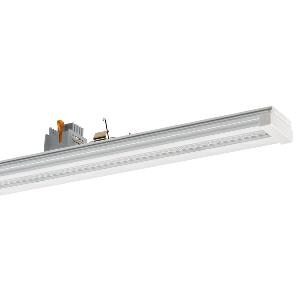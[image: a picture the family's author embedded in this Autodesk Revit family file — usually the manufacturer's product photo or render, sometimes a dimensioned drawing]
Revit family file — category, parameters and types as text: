
# Revit family: conveo_-_cvg_4500_840_xn-l_da_7_226848379-00804976_a8b3
name_source: partatom
category: Lighting Fixtures
units: mm (PartAtom-declared; Revit-internal decimal feet)

## family parameters
Cut with Voids When Loaded = No
Host = Face
Light Source = No
Part Type = Normal
Room Calculation Point = No
Round Connector Dimension = Use Diameter
Shared = No

## types (1)
- CONVEO - CVG 4500/840/xN-L/DA/7 (1 x LED, 4650 lm, 4000K)
    Apparent Load = 27 VA
    Approval mark = CE
    CIE Flux Codes = 84 95 99 100 100
    Color Rendering = 80-89
    Color Temperature = 4000K
    Control Gear = Electronic ballast
    Default Elevation = 1800 mm
    Description = CVG 4500/840/xN-L/DA/7|Continuous-row system|light source: LED|work equipment: Adjustable electronic ballast, digital DALI|connected load: 220-240 V, 50-60 Hz|Power consumption: approx. 27 W|luminous flux: 4650 lm|luminous efficacy: 172 lm/W|colour temperature: Cold white, ca. 4000 K|color rendering index (CRI): >= 80|chromaticity tolerance:  3 SDCM|System of protection: IP 54|class of protection: I|technology: Continuously dimmable|luminaire body|material: Aluminium|surface: Powder coatet|colour: White|lamp cover: Acrylic (PMMA), Satine|weight (net): approx. 1.9 kg|Fastening: Available separately|maximum ambient temperature: 50 ░C|glare control: Lens optics|Approval mark: VDE - ENEC|
    Frequency = 50 Hz
    Height = 70 mm
    Lamp = 1 x LED
    Lamp Light Flux = 4650 lm
    Lamp count = 1
    Length = 1500 mm
    Luminous efficacy = 172 lm/W
    Manufacturer = Waldmann
    ModVariant = No
    Model = 226848379-00804976
    Mounting Place = Ceiling
    Mounting Type = Pendant
    Number of Poles = 1
    OnlyDefault = Yes
    Power Factor = 1
    Product Name = CONVEO - CVG 4500/840/xN-L/DA/7
    Product group = Continuous-row system (industry)
    ProductGroupID = 301
    Protection Class = Protection class I
    Protection Degree = IP 54
    RLX_Detail_Level = 1
    RlxData = <blob elided: 100649 chars, md5=d7fdd995>
    Socket = socket
    Standby Power = 0 W
    System Light Flux = 4650 lm
    System Power = 27 W
    Type Comments = Product without accessories
    Type Image = 226848259-00804964_1l7.jpg
    URL = http://relux.com
    VarID = ---
    Voltage = 230 V
    Voltage Range = 220-240 V
    Weight = 0.00 kg
    Width = 64 mm

## geometry (parser evidence)
native form markers: Blend x4, Sweep x10
no freeform markers — native parametric forms only
